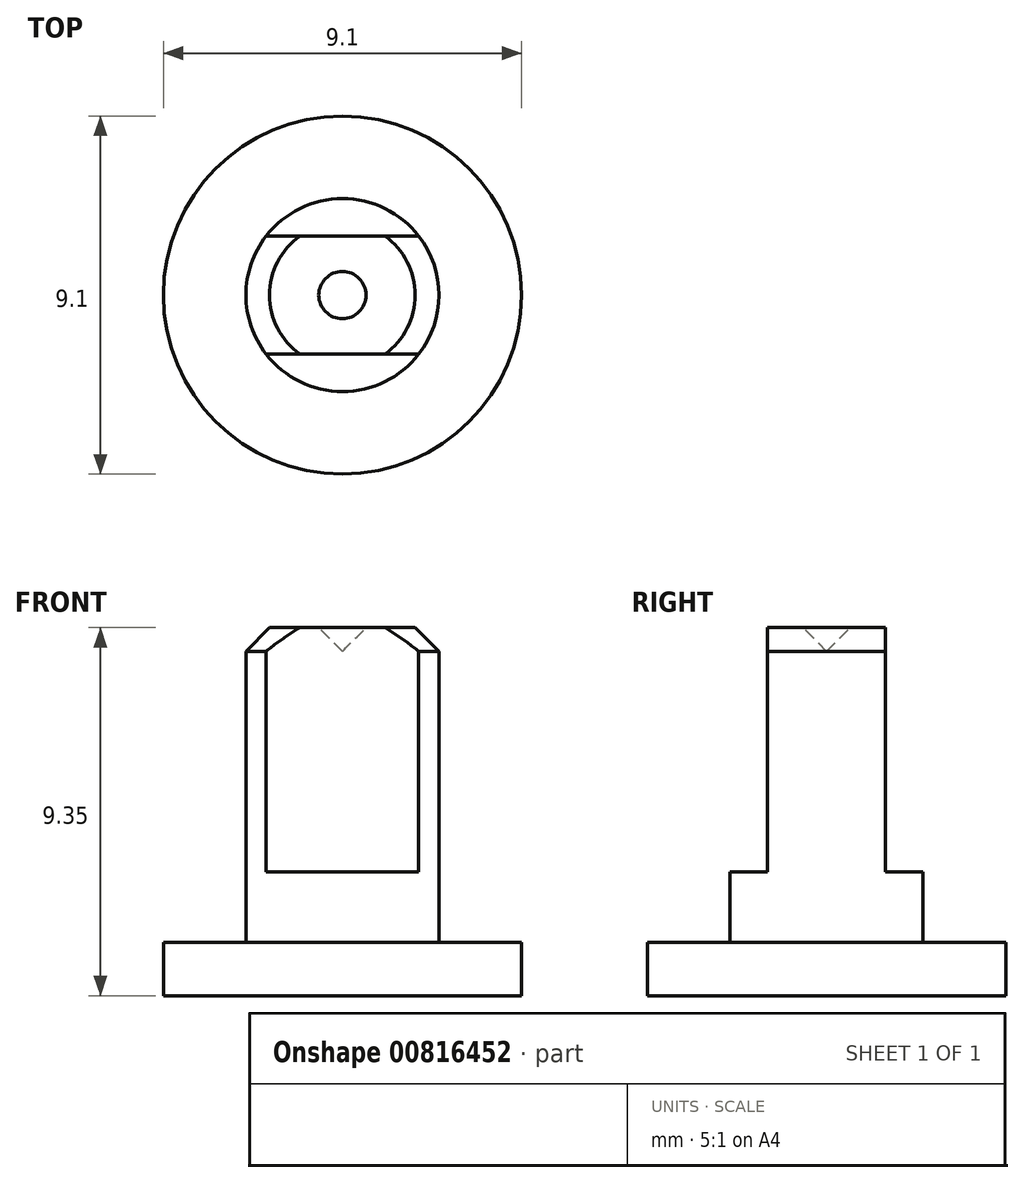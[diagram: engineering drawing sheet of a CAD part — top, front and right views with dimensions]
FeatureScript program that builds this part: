
annotation { "Feature Type Name" : "Feature", "Feature Type Description" : "" }
export const myFeature = defineFeature(function(context is Context, id is Id, definition is map)
    precondition{}
    {
        {
            var Q0;
            Q0=qCreatedBy(makeId("Front.planeOp"),FACE);
            var sketch = newSketch(context, id + "F0", { "sketchPlane" : qUnion([Q0])});
            skLineSegment(sketch, "E0", {"start": v(0, 0) * mm, "end": v(0, 8.75) * mm});
            skLineSegment(sketch, "E1", {"start": v(0.6, 9.35) * mm, "end": v(1.85, 9.35) * mm});
            skLineSegment(sketch, "E2", {"start": v(2.45, 8.75) * mm, "end": v(2.45, 1.35) * mm});
            skLineSegment(sketch, "E3", {"start": v(2.45, 1.35) * mm, "end": v(4.55, 1.35) * mm});
            skLineSegment(sketch, "E4", {"start": v(4.55, 1.35) * mm, "end": v(4.55, 0) * mm});
            skLineSegment(sketch, "E5", {"start": v(4.55, 0) * mm, "end": v(0, 0) * mm});
            skLineSegment(sketch, "E6", {"start": v(1.85, 9.35) * mm, "end": v(2.45, 8.75) * mm});
            skLineSegment(sketch, "E7", {"start": v(0.6, 9.35) * mm, "end": v(0, 8.75) * mm});
            skLineSegment(sketch, "E8", {"start": v(0, 8.75) * mm, "end": v(0, 13.35) * mm, "construction": true});
            skSolve(sketch);
        }
        {
            var Q0;
            Q0=makeQuery(id+"F0.imprint","IMPRINT",FACE,{"disambiguationData":[TD([[makeQuery(id+"F0.imprint","IMPRINT",EDGE,{"derivedFrom":sQuery(id+"F0.wireOp",EDGE,"E0")}),-1.0]])]});
            var Q1;
            Q1=sQuery(id+"F0.wireOp",EDGE,"E8");
            revolve(context, id + "F1", {"entities" : qUnion([Q0]), "axis" : qUnion([Q1]), "revolveType" : RevolveType.FULL, "surfaceOperationType" : NewSurfaceOperationType.NEW});
        }
        {
            var Q0;
            Q0=makeQuery(id+"F1.opRevolve","SWEPT_FACE",FACE,{"disambiguationData":[OSD([sQuery(id+"F0.wireOp",EDGE,"E1")])]});
            var sketch = newSketch(context, id + "F2", { "sketchPlane" : qUnion([Q0])});
            skLineSegment(sketch, "E9", {"start": v(-3.37, 1.5) * mm, "end": v(3.8, 1.5) * mm});
            skLineSegment(sketch, "E10", {"start": v(3.8, 1.5) * mm, "end": v(3.8, 4.5) * mm});
            skLineSegment(sketch, "E11", {"start": v(3.8, 4.5) * mm, "end": v(-3.37, 4.5) * mm});
            skLineSegment(sketch, "E12", {"start": v(-3.37, 4.5) * mm, "end": v(-3.37, 1.5) * mm});
            skLineSegment(sketch, "E13", {"start": v(0, 0) * mm, "end": v(9.16, 0) * mm, "construction": true});
            skLineSegment(sketch, "E14.MirrorCS", {"start": v(-3.37, -4.5) * mm, "end": v(-3.37, -1.5) * mm});
            skLineSegment(sketch, "E15.MirrorCS", {"start": v(3.8, -4.5) * mm, "end": v(-3.37, -4.5) * mm});
            skLineSegment(sketch, "E16.MirrorCS", {"start": v(3.8, -1.5) * mm, "end": v(3.8, -4.5) * mm});
            skLineSegment(sketch, "E17.MirrorCS", {"start": v(-3.37, -1.5) * mm, "end": v(3.8, -1.5) * mm});
            skSolve(sketch);
        }
        {
            var Q0;
            Q0=qSketchRegion(id+"F2",true);
            extrude(context, id + "F3", {"entities" : qUnion([Q0]), "operationType" : NewBodyOperationType.REMOVE, "oppositeDirection" : true, "depth" : 6.2 * mm});
        }
    });
